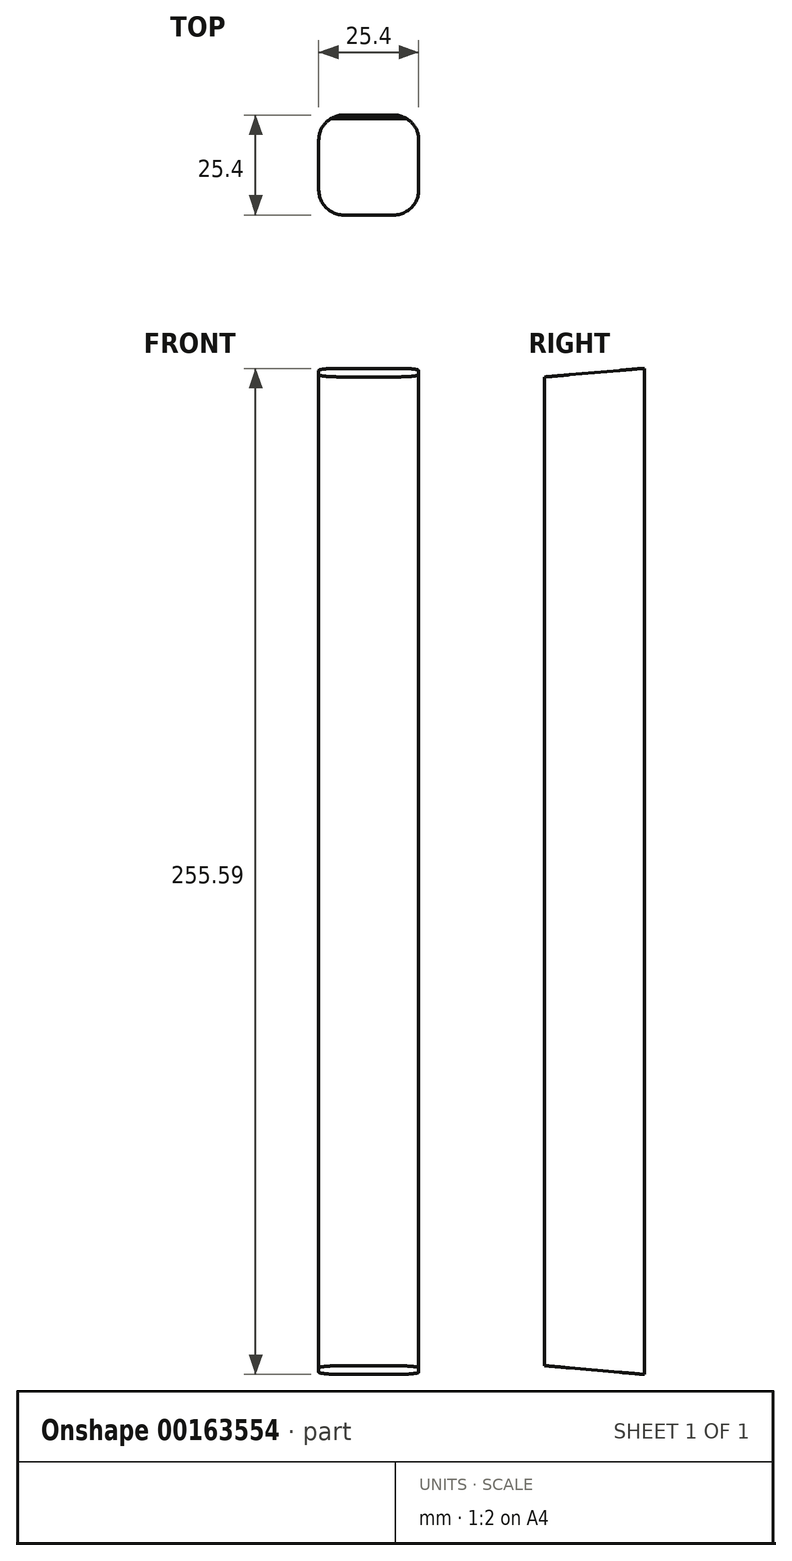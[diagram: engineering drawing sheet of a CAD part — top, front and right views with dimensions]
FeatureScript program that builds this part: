
annotation { "Feature Type Name" : "Feature", "Feature Type Description" : "" }
export const myFeature = defineFeature(function(context is Context, id is Id, definition is map)
    precondition{}
    {
        {
            var Q0;
            Q0=qCreatedBy(makeId("Top.planeOp"),FACE);
            var sketch = newSketch(context, id + "F0", { "sketchPlane" : qUnion([Q0])});
            skLineSegment(sketch, "E0.bottom", {"start": v(6.35, 12.7) * mm, "end": v(-6.35, 12.7) * mm});
            skLineSegment(sketch, "E0.top", {"start": v(6.35, -12.7) * mm, "end": v(-6.35, -12.7) * mm});
            skLineSegment(sketch, "E0.left", {"start": v(12.7, 6.35) * mm, "end": v(12.7, -6.35) * mm});
            skLineSegment(sketch, "E0.right", {"start": v(-12.7, 6.35) * mm, "end": v(-12.7, -6.35) * mm});
            skPoint(sketch, "E0.middle", {"position": v(0, 0) * mm});
            skPoint(sketch, "E1.visualSharp", {"position": v(-12.7, 12.7) * mm});
            skArc(sketch, "E1.filletArc", {"start": v(-6.35, 12.7) * mm, "mid": v(-10.84, 10.84) * mm, "end": v(-12.7, 6.35) * mm});
            skPoint(sketch, "E2.visualSharp", {"position": v(-12.7, -12.7) * mm});
            skArc(sketch, "E2.filletArc", {"start": v(-12.7, -6.35) * mm, "mid": v(-10.84, -10.84) * mm, "end": v(-6.35, -12.7) * mm});
            skPoint(sketch, "E3.visualSharp", {"position": v(12.7, -12.7) * mm});
            skArc(sketch, "E3.filletArc", {"start": v(6.35, -12.7) * mm, "mid": v(10.84, -10.84) * mm, "end": v(12.7, -6.35) * mm});
            skPoint(sketch, "E4.visualSharp", {"position": v(12.7, 12.7) * mm});
            skArc(sketch, "E4.filletArc", {"start": v(12.7, 6.35) * mm, "mid": v(10.84, 10.84) * mm, "end": v(6.35, 12.7) * mm});
            skSolve(sketch);
        }
        {
            var Q0;
            Q0=qSketchRegion(id+"F0",true);
            extrude(context, id + "F1", {"entities" : qUnion([Q0]), "depth" : 255.6 * mm, "offsetDistance" : 25.4 * mm});
        }
        {
            var Q0;
            Q0=qCreatedBy(makeId("Right.planeOp"),FACE);
            var sketch = newSketch(context, id + "F2", { "sketchPlane" : qUnion([Q0])});
            skLineSegment(sketch, "E5", {"start": v(12.7, 0) * mm, "end": v(-17.71, 2.66) * mm});
            skLineSegment(sketch, "E6", {"start": v(-17.71, 2.66) * mm, "end": v(-17.71, 0) * mm});
            skLineSegment(sketch, "E7", {"start": v(-17.71, 0) * mm, "end": v(12.7, 0) * mm});
            skSolve(sketch);
        }
        {
            var Q0;
            Q0=makeQuery(id+"F2.imprint","IMPRINT",FACE,{"disambiguationData":[TD([[makeQuery(id+"F2.imprint","IMPRINT",EDGE,{"derivedFrom":sQuery(id+"F2.wireOp",EDGE,"E5")}),1.0]])]});
            extrude(context, id + "F3", {"entities" : qUnion([Q0]), "operationType" : NewBodyOperationType.REMOVE, "endBound" : BoundingType.SYMMETRIC, "oppositeDirection" : true, "depth" : 25.4 * mm, "offsetDistance" : 25.4 * mm});
        }
        {
            var Q0;
            Q0=qCreatedBy(makeId("Right.planeOp"),FACE);
            var sketch = newSketch(context, id + "F4", { "sketchPlane" : qUnion([Q0])});
            skLineSegment(sketch, "E8", {"start": v(13.18, 255.71) * mm, "end": v(-13.45, 255.71) * mm});
            skLineSegment(sketch, "E9", {"start": v(-13.45, 255.71) * mm, "end": v(-13.45, 253.38) * mm});
            skLineSegment(sketch, "E10", {"start": v(-13.45, 253.38) * mm, "end": v(13.18, 255.71) * mm});
            skSolve(sketch);
        }
        {
            var Q0;
            Q0 = qSketchRegion(id + "F4", true);
            extrude(context, id + "F5", {"entities" : qUnion([Q0]), "operationType" : NewBodyOperationType.REMOVE, "endBound" : BoundingType.SYMMETRIC, "oppositeDirection" : true, "depth" : 25.4 * mm, "offsetDistance" : 25.4 * mm});
        }
    });
